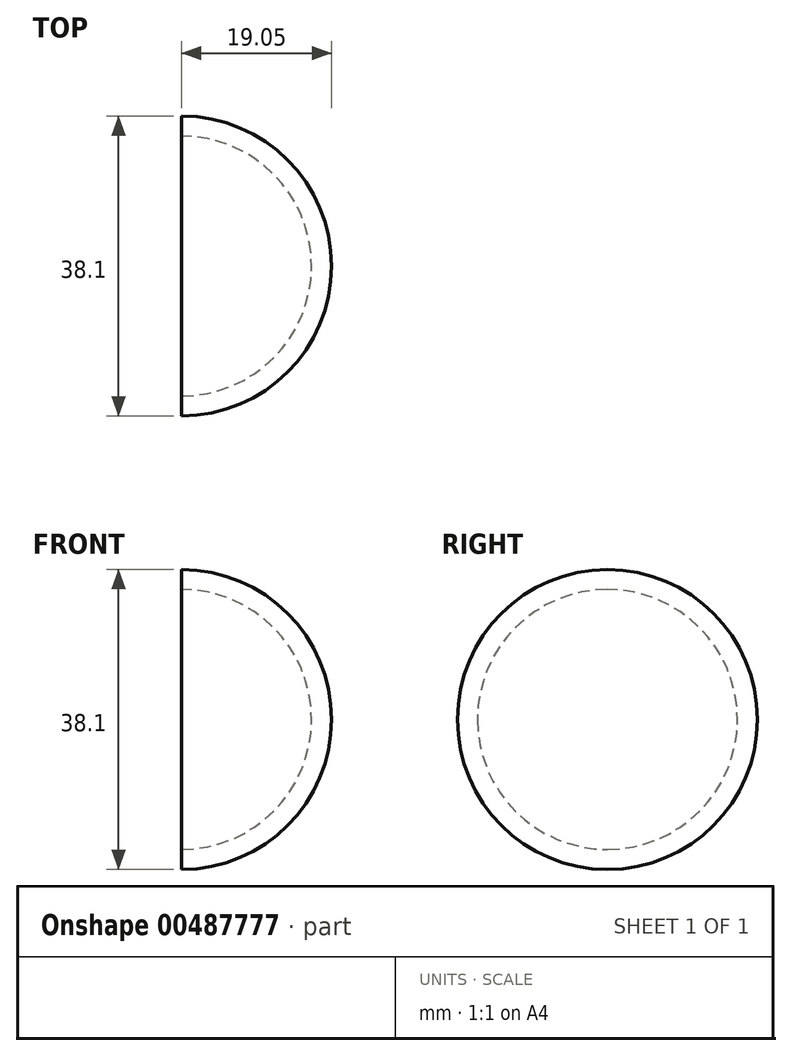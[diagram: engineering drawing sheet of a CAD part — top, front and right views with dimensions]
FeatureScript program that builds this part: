
annotation { "Feature Type Name" : "Feature", "Feature Type Description" : "" }
export const myFeature = defineFeature(function(context is Context, id is Id, definition is map)
    precondition{}
    {
        {
            var Q0;
            Q0=qCreatedBy(makeId("Front.planeOp"),FACE);
            var sketch = newSketch(context, id + "F0", { "sketchPlane" : qUnion([Q0])});
            skArc(sketch, "E0", {"start": v(0, -19.05) * mm, "mid": v(19.05, 0) * mm, "end": v(0, 19.05) * mm});
            skLineSegment(sketch, "E1", {"start": v(0, 0) * mm, "end": v(0, -19.05) * mm});
            skLineSegment(sketch, "E2", {"start": v(0, 0) * mm, "end": v(0, 19.05) * mm});
            skLineSegment(sketch, "E3", {"start": v(0, 0) * mm, "end": v(0, 44.32) * mm, "construction": true});
            skSolve(sketch);
        }
        {
            var Q0;
            Q0 = qSketchRegion(id + "F0", true);
            var Q1;
            Q1=sQuery(id+"F0.wireOp",EDGE,"E3");
            revolve(context, id + "F1", {"entities" : qUnion([Q0]), "axis" : qUnion([Q1]), "revolveType" : RevolveType.SYMMETRIC, "oppositeDirection" : true, "angle" : 180 * degree});
        }
        {
            var Q0;
            Q0=makeQuery(id+"F1.opRevolve","CAP_FACE",FACE,{"disambiguationData":[OSD([sQuery(id+"F0.wireOp",EDGE,"E0"),sQuery(id+"F0.wireOp",EDGE,"E1"),sQuery(id+"F0.wireOp",EDGE,"E2")])],"isStart":true});
            shell(context, id + "F2", {"entities" : qUnion([Q0]), "thickness" : 2.54 * mm});
        }
    });
